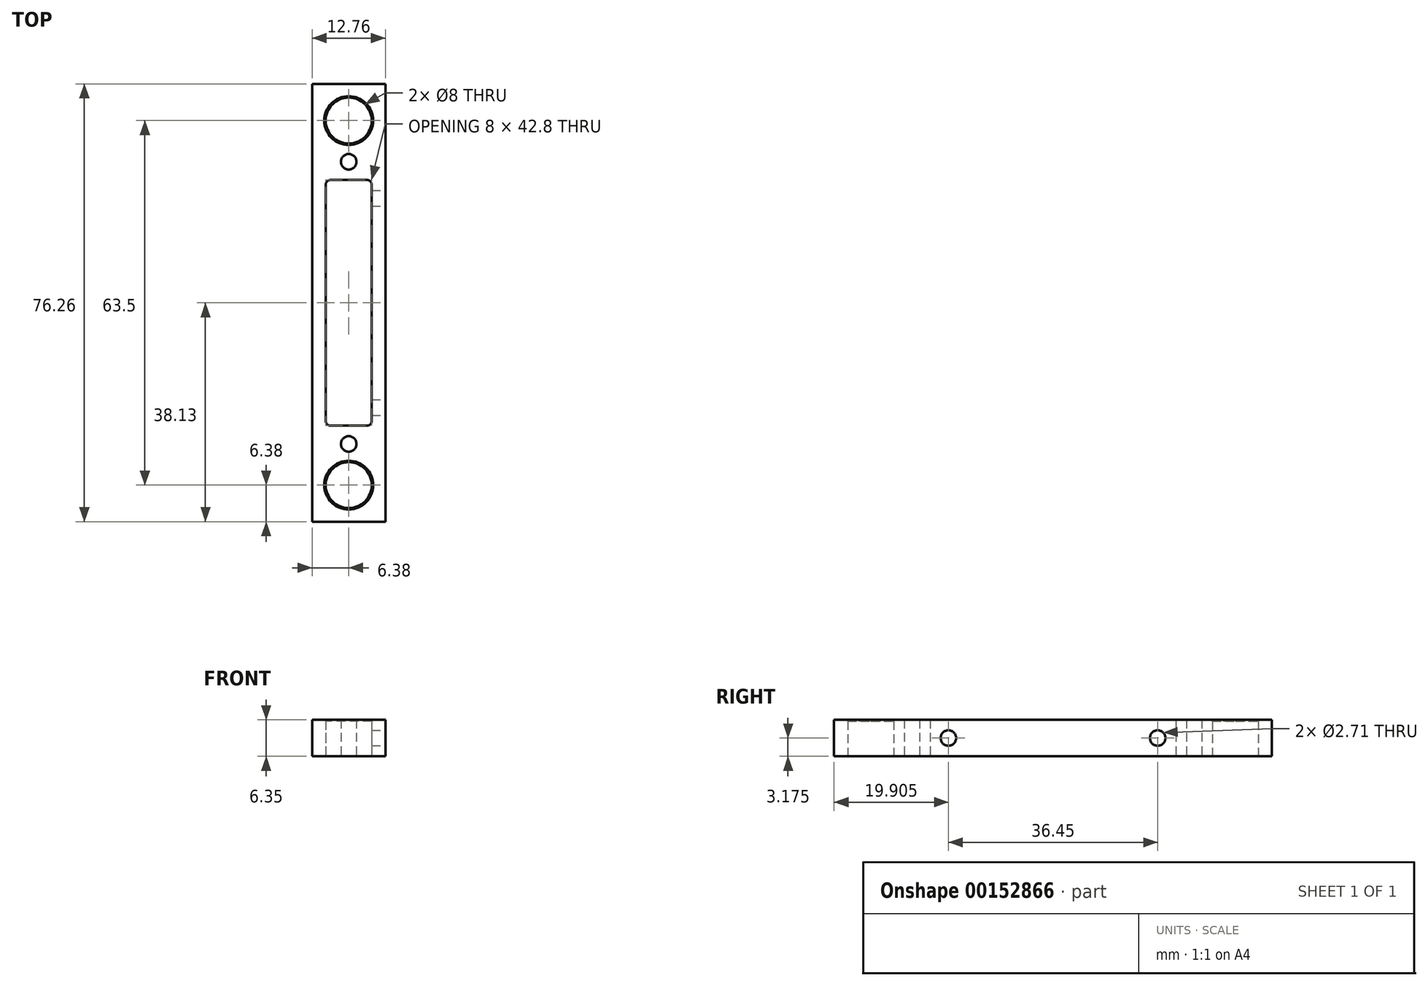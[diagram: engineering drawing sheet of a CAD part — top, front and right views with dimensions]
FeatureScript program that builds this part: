
annotation { "Feature Type Name" : "Feature", "Feature Type Description" : "" }
export const myFeature = defineFeature(function(context is Context, id is Id, definition is map)
    precondition{}
    {
        {
            var Q0;
            Q0=qCreatedBy(makeId("Top.planeOp"),FACE);
            var sketch = newSketch(context, id + "F0", { "sketchPlane" : qUnion([Q0])});
            skLineSegment(sketch, "E0.bottom", {"start": v(6.38, -38.13) * mm, "end": v(-6.38, -38.13) * mm});
            skLineSegment(sketch, "E0.top", {"start": v(6.38, 38.13) * mm, "end": v(-6.38, 38.13) * mm});
            skLineSegment(sketch, "E0.left", {"start": v(6.38, -38.13) * mm, "end": v(6.38, 38.13) * mm});
            skLineSegment(sketch, "E0.right", {"start": v(-6.38, -38.13) * mm, "end": v(-6.38, 38.13) * mm});
            skPoint(sketch, "E0.middle", {"position": v(0, 0) * mm});
            skLineSegment(sketch, "E1.bottom", {"start": v(4, -21.4) * mm, "end": v(-4, -21.4) * mm});
            skLineSegment(sketch, "E1.top", {"start": v(4, 21.4) * mm, "end": v(-4, 21.4) * mm});
            skLineSegment(sketch, "E1.left", {"start": v(4, -21.4) * mm, "end": v(4, 21.4) * mm});
            skLineSegment(sketch, "E1.right", {"start": v(-4, -21.4) * mm, "end": v(-4, 21.4) * mm});
            skLineSegment(sketch, "E2", {"start": v(0, 21.4) * mm, "end": v(0, 24.58) * mm, "construction": true});
            skLineSegment(sketch, "E3", {"start": v(0, 24.58) * mm, "end": v(0, 31.75) * mm, "construction": true});
            skLineSegment(sketch, "E4", {"start": v(0, 31.75) * mm, "end": v(0, 38.13) * mm, "construction": true});
            skCircle(sketch, "E5", {"center": v(0, 31.75) * mm, "radius": 4 * mm});
            skLineSegment(sketch, "E6", {"start": v(0, 31.75) * mm, "end": v(-6.38, 31.75) * mm, "construction": true});
            skCircle(sketch, "E7", {"center": v(0, 24.58) * mm, "radius": 3.18 * mm, "construction": true});
            skLineSegment(sketch, "E8", {"start": v(0, -38.13) * mm, "end": v(0, -31.75) * mm, "construction": true});
            skLineSegment(sketch, "E9", {"start": v(0, -31.75) * mm, "end": v(6.38, -31.75) * mm, "construction": true});
            skLineSegment(sketch, "E10", {"start": v(0, -31.75) * mm, "end": v(0, -24.58) * mm, "construction": true});
            skCircle(sketch, "E11", {"center": v(0, -31.75) * mm, "radius": 4 * mm});
            skCircle(sketch, "E12", {"center": v(0, -24.58) * mm, "radius": 1.35 * mm});
            skCircle(sketch, "E13", {"center": v(0, 24.58) * mm, "radius": 1.35 * mm});
            skSolve(sketch);
        }
        {
            var Q0;
            Q0=makeQuery(id+"F0.imprint","IMPRINT",FACE,{"disambiguationData":[TD([[makeQuery(id+"F0.imprint","IMPRINT",EDGE,{"derivedFrom":sQuery(id+"F0.wireOp",EDGE,"E0.bottom")}),-1.0]])]});
            extrude(context, id + "F1", {"entities" : qUnion([Q0]), "depth" : 6.35 * mm});
        }
        {
            var Q0;
            Q0=makeQuery(id+"F1.opExtrude","SWEPT_EDGE",EDGE,{"disambiguationData":[OSD([sQuery(id+"F0.wireOp",EDGE,"E1.bottom"),sQuery(id+"F0.wireOp",EDGE,"E1.left")])]});
            var Q1;
            Q1=makeQuery(id+"F1.opExtrude","SWEPT_EDGE",EDGE,{"disambiguationData":[OSD([sQuery(id+"F0.wireOp",EDGE,"E1.bottom"),sQuery(id+"F0.wireOp",EDGE,"E1.right")])]});
            var Q2;
            Q2=makeQuery(id+"F1.opExtrude","SWEPT_EDGE",EDGE,{"disambiguationData":[OSD([sQuery(id+"F0.wireOp",EDGE,"E1.top"),sQuery(id+"F0.wireOp",EDGE,"E1.right")])]});
            var Q3;
            Q3=makeQuery(id+"F1.opExtrude","SWEPT_EDGE",EDGE,{"disambiguationData":[OSD([sQuery(id+"F0.wireOp",EDGE,"E1.top"),sQuery(id+"F0.wireOp",EDGE,"E1.left")])]});
            fillet(context, id + "F2", {"entities" : qUnion([Q0, Q1, Q2, Q3]), "radius" : 0.8 * mm, "tangentPropagation" : true, "allowEdgeOverflow" : false});
        }
        {
            var Q0;
            Q0=makeQuery(id+"F1.opExtrude","CAP_EDGE",EDGE,{"disambiguationData":[OSD([sQuery(id+"F0.wireOp",EDGE,"E5")])],"isStart":false});
            var Q1;
            Q1=makeQuery(id+"F1.opExtrude","CAP_EDGE",EDGE,{"disambiguationData":[OSD([sQuery(id+"F0.wireOp",EDGE,"E11")])],"isStart":false});
            chamfer(context, id + "F3", {"entities" : qUnion([Q0, Q1]), "width" : 0.25 * mm, "tangentPropagation" : true});
        }
        {
            var Q0;
            Q0=makeQuery(id+"F1.opExtrude","SWEPT_FACE",FACE,{"disambiguationData":[OSD([sQuery(id+"F0.wireOp",EDGE,"E0.left")])]});
            var sketch = newSketch(context, id + "F4", { "sketchPlane" : qUnion([Q0])});
            skLineSegment(sketch, "E14", {"start": v(-21.4, 3.18) * mm, "end": v(-18.23, 3.18) * mm, "construction": true});
            skLineSegment(sketch, "E15", {"start": v(21.4, 3.18) * mm, "end": v(18.23, 3.17) * mm, "construction": true});
            skCircle(sketch, "E16", {"center": v(-18.23, 3.18) * mm, "radius": 1.35 * mm});
            skCircle(sketch, "E17", {"center": v(18.23, 3.17) * mm, "radius": 1.35 * mm});
            skSolve(sketch);
        }
        {
            var Q0;
            Q0 = qSketchRegion(id + "F4", true);
            var Q1;
            Q1=makeQuery(id+"F1.opExtrude","SWEPT_FACE",FACE,{"disambiguationData":[OSD([sQuery(id+"F0.wireOp",EDGE,"E1.left")])]});
            extrude(context, id + "F5", {"entities" : qUnion([Q0]), "operationType" : NewBodyOperationType.REMOVE, "endBound" : BoundingType.UP_TO_SURFACE, "oppositeDirection" : true, "endBoundEntityFace" : qUnion([Q1]), "depth" : 25.4 * mm});
        }
    });
